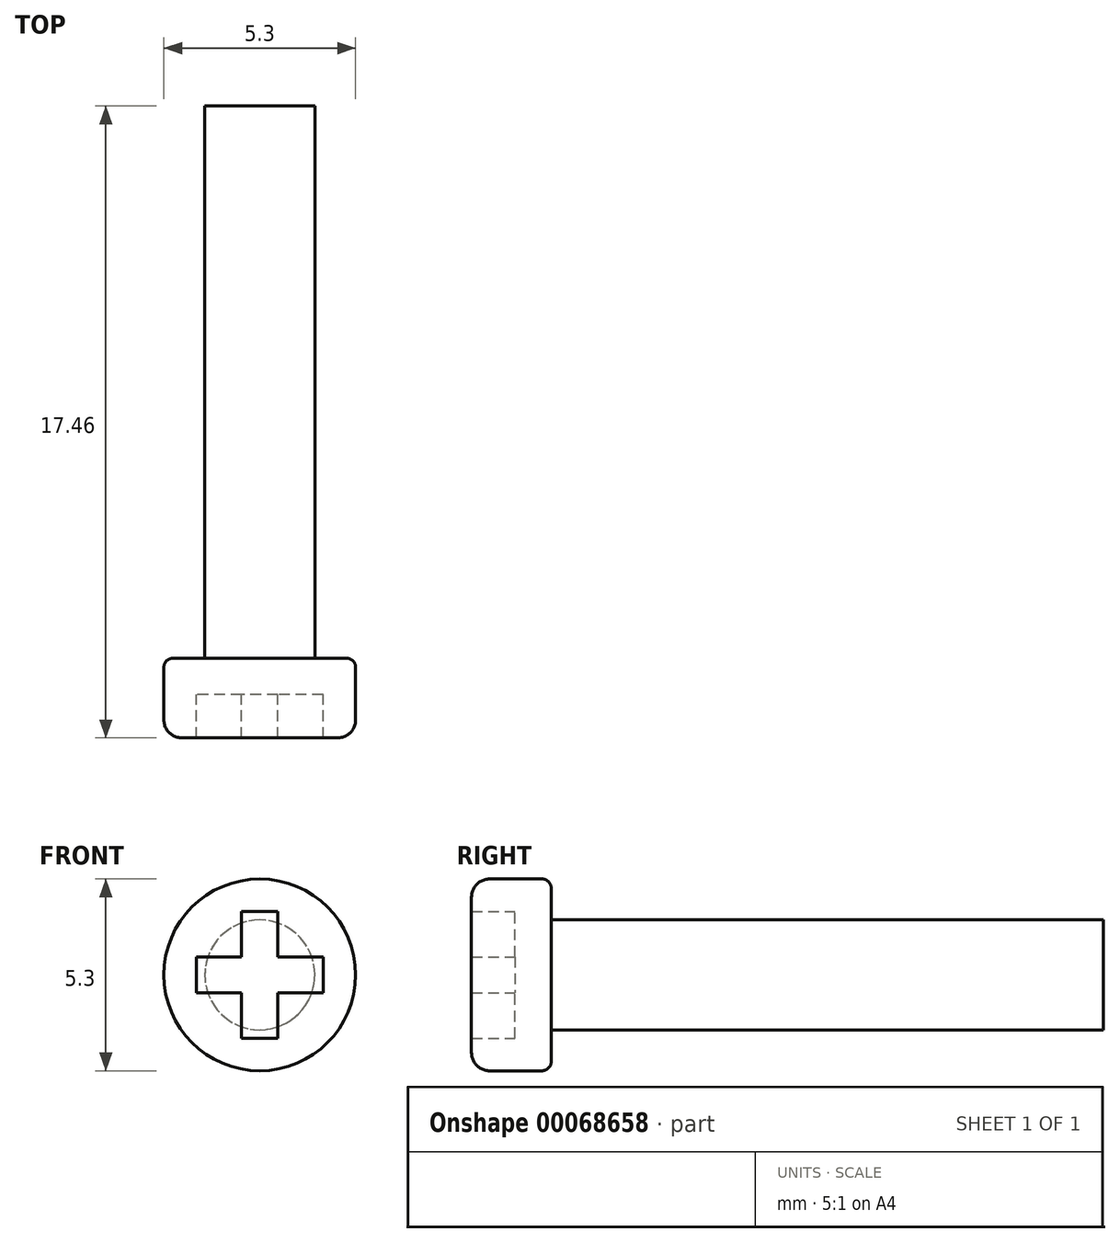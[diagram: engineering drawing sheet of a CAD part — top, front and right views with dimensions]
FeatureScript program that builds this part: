
annotation { "Feature Type Name" : "Feature", "Feature Type Description" : "" }
export const myFeature = defineFeature(function(context is Context, id is Id, definition is map)
    precondition{}
    {
        {
            var Q0;
            Q0=qCreatedBy(makeId("Front.planeOp"),FACE);
            var sketch = newSketch(context, id + "F0", { "sketchPlane" : qUnion([Q0])});
            skCircle(sketch, "E0", {"center": v(0, 0) * mm, "radius": 2.65 * mm});
            skLineSegment(sketch, "E1.rect.bottom", {"start": v(0.5, -1.75) * mm, "end": v(-0.5, -1.75) * mm});
            skLineSegment(sketch, "E1.rect.top", {"start": v(0.5, 1.75) * mm, "end": v(-0.5, 1.75) * mm});
            skLineSegment(sketch, "E1.rect.left", {"start": v(0.5, -1.75) * mm, "end": v(0.5, 1.75) * mm});
            skLineSegment(sketch, "E1.rect.right", {"start": v(-0.5, -1.75) * mm, "end": v(-0.5, 1.75) * mm});
            skLineSegment(sketch, "E2.rect.bottom", {"start": v(1.75, 0.5) * mm, "end": v(-1.75, 0.5) * mm});
            skLineSegment(sketch, "E2.rect.top", {"start": v(1.75, -0.5) * mm, "end": v(-1.75, -0.5) * mm});
            skLineSegment(sketch, "E2.rect.left", {"start": v(1.75, 0.5) * mm, "end": v(1.75, -0.5) * mm});
            skLineSegment(sketch, "E2.rect.right", {"start": v(-1.75, 0.5) * mm, "end": v(-1.75, -0.5) * mm});
            skSolve(sketch);
        }
        {
            var Q0;
            Q0=makeQuery(id+"F0.imprint","IMPRINT",FACE,{"disambiguationData":[TD([[makeQuery(id+"F0.imprint","IMPRINT",EDGE,{"derivedFrom":sQuery(id+"F0.wireOp",EDGE,"E0")}),1.0]])]});
            extrude(context, id + "F1", {"entities" : qUnion([Q0]), "depth" : 2.2 * mm});
        }
        {
            var Q0;
            {var subQ0=sQuery(id+"F0.wireOp",EDGE,"E1.rect.top");Q0=makeQuery(id+"F0.imprint","IMPRINT",FACE,{"disambiguationData":[TD([[makeQuery(id+"F0.imprint","IMPRINT",EDGE,{"derivedFrom":subQ0}),1.0]])]});}
            var Q1;
            {var subQ5=sQuery(id+"F0.wireOp",EDGE,"E2.rect.left");Q1=makeQuery(id+"F0.imprint","IMPRINT",FACE,{"disambiguationData":[TD([[makeQuery(id+"F0.imprint","IMPRINT",EDGE,{"derivedFrom":subQ5}),-1.0]])]});}
            var Q2;
            {var subQ5=sQuery(id+"F0.wireOp",EDGE,"E2.rect.right");Q2=makeQuery(id+"F0.imprint","IMPRINT",FACE,{"disambiguationData":[TD([[makeQuery(id+"F0.imprint","IMPRINT",EDGE,{"derivedFrom":subQ5}),1.0]])]});}
            var Q3;
            {var subQ0=sQuery(id+"F0.wireOp",EDGE,"E2.rect.top");var subQ1=sQuery(id+"F0.wireOp",EDGE,"E1.rect.left");var subQ2=makeQuery(id+"F0.imprint","INTERSECT",VERTEX,{"derivedFrom":[subQ1,subQ0]});Q3=makeQuery(id+"F0.imprint","IMPRINT",FACE,{"disambiguationData":[TD([[makeQuery(id+"F0.imprint","IMPRINT",EDGE,{"disambiguationData":[TD([[subQ2,-1.0]])],"derivedFrom":subQ1}),1.0]])]});}
            var Q4;
            {var subQ0=sQuery(id+"F0.wireOp",EDGE,"E1.rect.bottom");Q4=makeQuery(id+"F0.imprint","IMPRINT",FACE,{"disambiguationData":[TD([[makeQuery(id+"F0.imprint","IMPRINT",EDGE,{"derivedFrom":subQ0}),-1.0]])]});}
            extrude(context, id + "F2", {"entities" : qUnion([Q0, Q1, Q2, Q3, Q4]), "operationType" : NewBodyOperationType.ADD, "depth" : 1 * mm});
        }
        {
            var Q0;
            Q0=makeQuery(id+"F1.opExtrude","CAP_EDGE",EDGE,{"disambiguationData":[OSD([sQuery(id+"F0.wireOp",EDGE,"E0")])],"isStart":false});
            fillet(context, id + "F3", {"entities" : qUnion([Q0]), "radius" : .5 * mm, "tangentPropagation" : true, "allowEdgeOverflow" : false});
        }
        {
            var Q0;
            Q0=makeQuery(id+"F1.opExtrude","CAP_EDGE",EDGE,{"disambiguationData":[OSD([sQuery(id+"F0.wireOp",EDGE,"E0")])],"isStart":true});
            fillet(context, id + "F4", {"entities" : qUnion([Q0]), "radius" : .25 * mm, "tangentPropagation" : true, "allowEdgeOverflow" : false});
        }
        {
            var Q0;
            {var subQ0=sQuery(id+"F0.wireOp",EDGE,"E2.rect.right");var subQ1=sQuery(id+"F0.wireOp",EDGE,"E2.rect.left");var subQ2=sQuery(id+"F0.wireOp",EDGE,"E2.rect.top");var subQ3=sQuery(id+"F0.wireOp",EDGE,"E2.rect.bottom");var subQ4=sQuery(id+"F0.wireOp",EDGE,"E1.rect.right");var subQ5=sQuery(id+"F0.wireOp",EDGE,"E1.rect.left");var subQ6=sQuery(id+"F0.wireOp",EDGE,"E1.rect.top");var subQ7=sQuery(id+"F0.wireOp",EDGE,"E1.rect.bottom");Q0=makeQuery(id+"F2.boolean.opBoolean","MERGE",FACE,{"derivedFrom":[makeQuery(id+"F1.opExtrude","CAP_FACE",FACE,{"disambiguationData":[OSD([sQuery(id+"F0.wireOp",EDGE,"E0"),subQ7,subQ6,subQ5,subQ4,subQ3,subQ2,subQ1,subQ0])],"isStart":true}),makeQuery(id+"F2.opExtrude","CAP_FACE",FACE,{"disambiguationData":[OSD([subQ7,subQ6,subQ5,subQ4,subQ3,subQ2,subQ1,subQ0])],"isStart":true})]});}
            var sketch = newSketch(context, id + "F5", { "sketchPlane" : qUnion([Q0])});
            skCircle(sketch, "E3", {"center": v(0, 0) * mm, "radius": 1.52 * mm});
            skSolve(sketch);
        }
        {
            var Q0;
            Q0=makeQuery(id+"F5.imprint","IMPRINT",FACE,{"disambiguationData":[TD([[makeQuery(id+"F5.imprint","IMPRINT",EDGE,{"derivedFrom":sQuery(id+"F5.wireOp",EDGE,"E3")}),1.0]])]});
            extrude(context, id + "F6", {"entities" : qUnion([Q0]), "operationType" : NewBodyOperationType.ADD, "depth" : 15.26 * mm});
        }
    });
